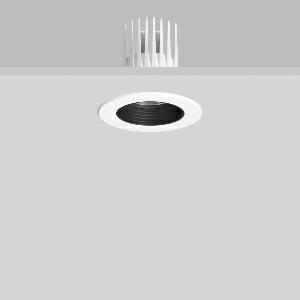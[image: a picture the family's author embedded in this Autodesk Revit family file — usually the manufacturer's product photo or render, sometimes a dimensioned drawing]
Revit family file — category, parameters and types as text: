
# Revit family: heledon_mini_e_901753_002_76_ab46
name_source: partatom
category: Lighting Fixtures
units: mm (PartAtom-declared; Revit-internal decimal feet)

## family parameters
Cut with Voids When Loaded = No
Host = Face
Light Source = No
Part Type = Normal
Room Calculation Point = No
Round Connector Dimension = Use Diameter
Shared = No

## types (1)
- HELEDON mini E (1 x LED Modul 930, 2850 lm, 3000)
    Apparent Load = 29 VA
    Approval mark = CE
    CIE Flux Codes = 98 100 100 100 100
    Color Rendering = 90
    Color Temperature = 3000
    Default Elevation = 1800 mm
    Description = Series: HELEDON mini
Round recessed downlight. Housing: die-cast aluminium, powder-coated. Black plastic ring and recessed LED to prevent glare from the side. Optical assembly with lens made of plastic (polycarbonate) for the best homogeneous light distribution - can be changed without tools. Best colour rendering index Ra>90. Suitable for Recessed ceiling mounting. Installation without tools thanks to spring fastening system. Including separate LED converter with connecting cable 600 mm.High quality converter without flickering and stroboscopic effect. Through-wiring box (5 pole) available as accessory. The following accessories can be mounted without use of tools: interchangeable lenses, decorative glasses, honeycomb louvre, clear and frosted diffusers, white interchangeable plastic ring. 
Colour: traffic white, matt (RAL 9016)
Diameter: 124 mm
Height: 3 mm
Cut-out diameter: 114 mm
Recess height: 170 mm
Luminaire: recess height: 120 mm
Lamp: LED
Socket: without socket
Colour temperature: 3000K
Colour rendering index (CRI): 92
System power: 29 W
Rated luminous flux: 2850 lm
Luminous efficiency: 98 lm/W
Control gear: Converter, dimmable, DALI
Protection class: II
Type of protection: IP 20
    Height = 0 mm  [stored 0 ft]
    Lamp = 1 x LED Modul 930
    Lamp Light Flux = 2850 lm
    Lamp count = 1
    Length = 124 mm  [stored 0.406824 ft]
    Lifetime = 50000 h
    Luminous efficacy = 98 lm/W
    Manufacturer = RZB
    ModVariant = No
    Model = 901753.002.76
    Mounting Place = Ceiling
    Mounting Type = Recessed
    Number of Poles = 1
    OnlyDefault = Yes
    Power Factor = 1
    Product Name = HELEDON mini E
    Product group = Recessed downlights
    ProductGroupID = 402
    Protection Class = Protection class II
    Protection Degree = IP 20
    RLX_Detail_Level = 1
    RLX_Emergency_Light_Flux = 0 lm
    RLX_Emergency_Type = 0
    RLX_Emergency_Type_DB = No
    RlxData = <blob elided: 125889 chars, md5=7af871ac>
    Socket = socket
    Standby Power = 0 W
    System Light Flux = 2850 lm
    System Power = 29 W
    Type Comments = Product without accessories
    Type Image = 901656.002.jpg
    URL = http://relux.com
    VarID = ---
    Voltage = 230 V
    Voltage Range = 220-240 V
    Weight = 0.00 kg
    Width = 0 mm  [stored 0 ft]

note: [stored X ft] marks values corroborated as IEEE doubles in the binary element streams (Revit-internal decimal feet)

## geometry (parser evidence)
native form markers: Blend x4, Sweep x11
no freeform markers — native parametric forms only
